# Revit family: RN 80047 Optipress-Aquaplus-Winkelverschraubung
name_source: partatom
category: Rohrformteile
units: mm (PartAtom-declared; Revit-internal decimal feet)

## family parameters
Arbeitsebenenbasiert = Nein
Beim Laden mit Abzugskörper schneiden = Nein
Bemaßung runder Anschluss = Durchmesser verwenden
Gemeinsam genutzt = Nein
Immer vertikal = Ja
Teiletyp = Verbindung

## types (8) — shared parameters
1.010.00.2 Blattnummer der Richtlinie = 29
1.010.00.3 Ausgabedatum (Monat) der Richtlinie = 201308
1.010.00.4 Herstellername = R. Nussbaum AG
1.010.00.5 Revisionsdatum der Datei = 20190521
1.010.00.6 Webadresse des Herstellers = http://www.nussbaum.ch
1.100.00.4 Produktbezeichnung = Versorgung
1.110.00.2 Index = 4
1.110.00.4 Produktbezeichnung = Optipress
1.960/3L.00.8 Link (URL) = https://www.nussbaum.ch
29.700.00.4 Produktname = Optipress-Aquaplus-Winkelverschraubung, mit Innengewinde
29.700.00.5 Produktkennung = 2
29.700.00.6 Querschnittsform = 1
29.700.00.7 Nennweitensystem = DN
29.700.00.8 Nenndrucksystem = PN
29.710.02.4 Nenndruck = 16
29.710.02.5 max. zul. Überdruck [hPa] = 1600
29.710.02.7 max. zul. Dauer-Betriebsdruck [hPa] = 1600
29.710.02.9 max. zul. Dauer-Betriebstemperatur [°C] = 95
Connector Visibility = Nein
EnclosingSpace Visibility = Nein

## per-type parameters (varying)
| type | 1.800.00.3 TGA-Nummer | 1.810.00.3 Hersteller-Bestellnummer | 1.810.00.4 DATANORM-Nummer | 1.810.00.5 StLB-Nummer | 1.810.00.6 GTIN-Nummer | 29.710.02.10 Formstück-Gewicht [kg] | 29.710.02.3 Benennung | CONNECTOR0_DIAMETER_dZ_0r | CONNECTOR0_dZ_01 | CONNECTOR0_ref_dZ | CONNECTOR1_DIAMETER_dX_0r | CONNECTOR1_dX_00 | CONNECTOR1_dX_01 | CONNECTOR1_ref_dX | CONNECTOR1_ref_dZ | R. Nussbaum AG 80047.22 de Visibility | R. Nussbaum AG 80047.23 de Visibility | R. Nussbaum AG 80047.25 de Visibility | R. Nussbaum AG 80047.26 de Visibility | R. Nussbaum AG 80047.29 de Visibility | R. Nussbaum AG 80047.31 de Visibility | R. Nussbaum AG 80047.33 de Visibility | R. Nussbaum AG 80047.34 de Visibility |
| 80047.22, Optipress-Aquaplus-Winkelverschraubung, mit Innengewinde, DN=12x15, L=63, Rp=½ | 01900400000000000000000000000000000000000000000029000000000000000001 | 80047.22 | 80047.22 | 266.512 | 7612945052131 | 0.14 | Optipress-Aquaplus-Winkelverschraubung, mit Innengewinde, DN=12x15, L=63, Rp=½ | 12 mm  [stored 0.0393701 ft] | 22 mm | 22 mm | 15 mm  [stored 0.0492126 ft] | 20 mm | 33 mm | 20 mm | 63 mm | Ja | Nein | Nein | Nein | Nein | Nein | Nein | Nein |
| 80047.23, Optipress-Aquaplus-Winkelverschraubung, mit Innengewinde, DN=15, L=63, Rp=½ | 01900400000000000000000000000000000000000000000029000000000000000002 | 80047.23 | 80047.23 | 266.513 | 7612945052148 | 0.14 | Optipress-Aquaplus-Winkelverschraubung, mit Innengewinde, DN=15, L=63, Rp=½ | 15 mm  [stored 0.0492126 ft] | 22 mm | 22 mm | 15 mm  [stored 0.0492126 ft] | 20 mm | 33 mm | 20 mm | 63 mm | Nein | Ja | Nein | Nein | Nein | Nein | Nein | Nein |
| 80047.25, Optipress-Aquaplus-Winkelverschraubung, mit Innengewinde, DN=20, L=71, Rp=¾ | 01900400000000000000000000000000000000000000000029000000000000000003 | 80047.25 | 80047.25 |  | 7612945052162 | 0.22 | Optipress-Aquaplus-Winkelverschraubung, mit Innengewinde, DN=20, L=71, Rp=¾ | 20 mm | 24 mm  [stored 0.0787402 ft] | 24 mm  [stored 0.0787402 ft] | 20 mm | 24 mm  [stored 0.0787402 ft] | 39 mm  [stored 0.127953 ft] | 24 mm  [stored 0.0787402 ft] | 71 mm | Nein | Nein | Ja | Nein | Nein | Nein | Nein | Nein |
| 80047.26, Optipress-Aquaplus-Winkelverschraubung, mit Innengewinde, DN=20x25, L=74, Rp=1 | 01900400000000000000000000000000000000000000000029000000000000000004 | 80047.26 | 80047.26 | 266.514 | 7612945052179 | 0.28 | Optipress-Aquaplus-Winkelverschraubung, mit Innengewinde, DN=20x25, L=74, Rp=1 | 20 mm | 24 mm  [stored 0.0787402 ft] | 24 mm  [stored 0.0787402 ft] | 20 mm | 29 mm  [stored 0.0951444 ft] | 44 mm | 29 mm  [stored 0.0951444 ft] | 74 mm | Nein | Nein | Nein | Ja | Nein | Nein | Nein | Nein |
| 80047.29, Optipress-Aquaplus-Winkelverschraubung, mit Innengewinde, DN=25, L=81, Rp=1 | 01900400000000000000000000000000000000000000000029000000000000000005 | 80047.29 | 80047.29 | 266.515 | 7612945052186 | 0.38 | Optipress-Aquaplus-Winkelverschraubung, mit Innengewinde, DN=25, L=81, Rp=1 | 25 mm  [stored 0.082021 ft] | 24 mm  [stored 0.0787402 ft] | 24 mm  [stored 0.0787402 ft] | 25 mm  [stored 0.082021 ft] | 30 mm  [stored 0.0984252 ft] | 47 mm | 30 mm  [stored 0.0984252 ft] | 81 mm | Nein | Nein | Nein | Nein | Ja | Nein | Nein | Nein |
| 80047.31, Optipress-Aquaplus-Winkelverschraubung, mit Innengewinde, DN=32, L=86, Rp=1¼ | 01900400000000000000000000000000000000000000000029000000000000000006 | 80047.31 | 80047.31 | 266.516 | 7612945052193 | 0.493 | Optipress-Aquaplus-Winkelverschraubung, mit Innengewinde, DN=32, L=86, Rp=1¼ | 32 mm | 26 mm | 26 mm | 32 mm | 38 mm | 57 mm | 38 mm | 86 mm | Nein | Nein | Nein | Nein | Nein | Ja | Nein | Nein |
| 80047.33, Optipress-Aquaplus-Winkelverschraubung, mit Innengewinde, DN=40, L=108, Rp=1½ | 01900400000000000000000000000000000000000000000029000000000000000007 | 80047.33 | 80047.33 | 266.517 | 7612945052209 | 0.74 | Optipress-Aquaplus-Winkelverschraubung, mit Innengewinde, DN=40, L=108, Rp=1½ | 40 mm | 36 mm | 36 mm | 40 mm | 40 mm | 59 mm | 40 mm | 108 mm | Nein | Nein | Nein | Nein | Nein | Nein | Ja | Nein |
| 80047.34, Optipress-Aquaplus-Winkelverschraubung, mit Innengewinde, DN=50, L=124, Rp=2 | 01900400000000000000000000000000000000000000000029000000000000000008 | 80047.34 | 80047.34 | 266.518 | 7612945052216 | 1.276 | Optipress-Aquaplus-Winkelverschraubung, mit Innengewinde, DN=50, L=124, Rp=2 | 50 mm | 40 mm | 40 mm | 50 mm | 45 mm | 69 mm | 45 mm | 125 mm | Nein | Nein | Nein | Nein | Nein | Nein | Nein | Ja |

note: column(s) folded — value = type name in every type: 1.800.00.4 Kommentarfeld

note: [stored X ft] marks values corroborated as IEEE doubles in the binary element streams (Revit-internal decimal feet)

## geometry (parser evidence)
native form markers: Sweep x2
no freeform markers — native parametric forms only
